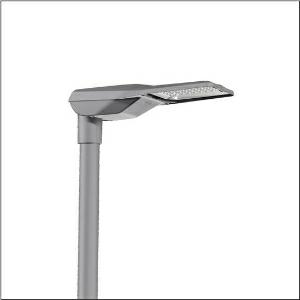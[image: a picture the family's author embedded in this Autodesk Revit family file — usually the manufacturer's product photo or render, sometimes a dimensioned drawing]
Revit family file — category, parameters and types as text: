
# Revit family: streetlight_sl_21_iq_mini___st0_8a_5xe2c41g08gb_95af
name_source: partatom
category: Lighting Fixtures
units: mm (PartAtom-declared; Revit-internal decimal feet)

## family parameters
Cut with Voids When Loaded = No
Host = Face
Light Source = No
Part Type = Normal
Room Calculation Point = No
Round Connector Dimension = Use Diameter
Shared = No

## types (1)
- --- (1 x LED, 5920 lm, 37.1 W, 4000K)
    Apparent Load = 37 VA
    CIE Flux Codes = 38 75 97 100 100
    Color Rendering = 70
    Color Temperature = 4000K
    Default Elevation = 1800 mm
    Description = Streetlight SL 21 iQ mini, mast luminaire, primary light control with lens, of PMMA, primary optical cover: cover, of toughened safety glass, transparent, light distribution: ST0.8a, light emission: direct distribution, primary light characteristic: asymmetric, installation type: post-top, side-entry, LED, High Power LED, rated luminous flux: 5.920lm, luminous efficacy: 160lm/W, light colour: 740, colour temperature: 4000K, control gear: iQ Street-Remote, control: Street-Remote, Auto-Match, Temp-Guard, Lumen-Switch, Night-Set, Smart-Wire, Light-Fading, Desk-Remote (wireless, voltage-free reading and setting of iQ features in the workshop via application-optimized NFC function/RFID function), optimised constant luminous flux control (CLO 2.0), pre-setting: linear dimming characteristic, mains connection: 220..240V, AC, 50/60Hz, start of lifetime: 37W, end of service life: 39W, reduction: 18W, luminaire housing, of diecast aluminium, powder-coated, SITECO metallic grey (DB 702S), corrosivity category C5 high according to DIN EN ISO 12944, please order mast flange separately, inclination adjustable: 0°, 5°, 10°, 15°, sealing non-destructively replaceable, multi-level sealing system, length: 628mm, width: 235mm, height: 110mm, mast flange for spigot size: 42mm (side-entry): 5XC10008XM4, 60/48mm (side-entry/post-top): 5XC10108XM2, 76/60mm (side-entry/post-top): 5XC10108XM1, mounting height: 4..8m, protection rating (complete): IP66, insulation class (complete): insulation class II (safety insulation), certification: CE, ENEC, ENEC+, VDE, impact resistance: IK10, permissible operating ambient temperature for outdoor applications: -40..+50°C, standard-compliant lighting for roads and squares, packaging unit: 1 piece

Light Distribution: ST0.8a
    Height = 110 mm
    Lamp = 1 x LED
    Lamp Light Flux = 5920 lm
    Lamp Power = 37.1 W
    Lamp count = 1
    Length = 625 mm
    Luminous efficacy = 160 lm/W
    Manufacturer = Siteco
    ModVariant = No
    Model = 5XE2C41G08GB
    Number of Poles = 1
    OnlyDefault = Yes
    Power Factor = 1
    Product Name = Streetlight SL 21 iQ mini | ST0.8a
    Product group = mast luminaire | pylon top
    ProductGroupID = 6100
    Protection Class = Protection class II
    Protection Degree = IP 66
    RLX_Detail_Level = 1
    RLX_Emergency_Light_Flux = 0 lm
    RLX_Emergency_Type = 0
    RLX_Emergency_Type_DB = No
    RlxData = <blob elided: 26349 chars, md5=72095cef>
    Socket = socket
    Standby Power = 0 W
    System Light Flux = 5920 lm
    System Power = 37 W
    Type Comments = factory setting: luminous flux: 100 % | dim-lin: 254 | 385 mA
    Type Image = l_1003519.jpg
    URL = http://relux.com
    VarID = @adj_183067
    Voltage = 0 V
    Weight = 0.00 kg
    Width = 234 mm

## geometry (parser evidence)
native form markers: Blend x4, Sweep x11
no freeform markers — native parametric forms only
